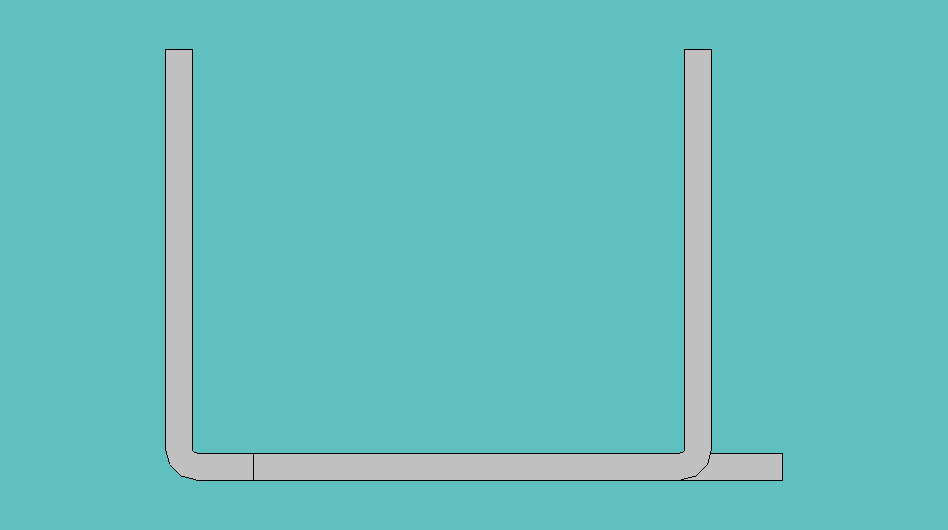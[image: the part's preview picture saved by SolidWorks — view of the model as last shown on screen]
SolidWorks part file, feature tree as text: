
SOLIDWORKS PART (.sldprt)
format: sldprt  version: not decoded by parser v0  size: 322,560 bytes
history: native  units: mm
features: sketch x3, extrude x3, fillet x2, material x1 (+12 scaffold rows collapsed)
feature tree (21):
  scaffold x12  (default folders/planes/origin — collapsed)
  material  "Material <not specified>"
  sketch  "Sketch1"  dims[D1=20.2438mm]
  extrude  "Extrude1"  Depth=1.524mm
  sketch  "Sketch3"  dims[D1=14.2748mm]
  extrude  "Extrude3"  Depth=1.524mm
  extrude  "Extrude4"  [1 undecoded]
  sketch  "Sketch3<3>"  dims[D1=1.524mm]
  fillet  "Fillet4"  Radius=1.778mm
  fillet  "Fillet5"  Radius=0.254mm
decode coverage: 7 of 8 modeling features carry decoded parameters
note: 1 parameter value undecoded
note: suppression state not decoded; provenance and decode notes live in map.json
